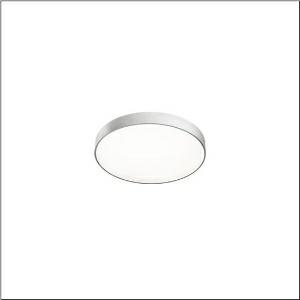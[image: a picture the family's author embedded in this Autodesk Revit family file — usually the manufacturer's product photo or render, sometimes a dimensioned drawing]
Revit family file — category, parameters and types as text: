
# Revit family: round_21_s_51mr34gd0321s
name_source: partatom
category: Lighting Fixtures
units: mm (PartAtom-declared; Revit-internal decimal feet)

## family parameters
Cut with Voids When Loaded = No
Host = Face
Light Source = No
Part Type = Normal
Room Calculation Point = No
Round Connector Dimension = Use Diameter
Shared = No

## types (1)
- Round 21 S (1 x LED, 3930 lm, 28.3 W, 3000K)
    Apparent Load = 28 VA
    CIE Flux Codes = 49 80 96 79 100
    Color Rendering = 80
    Color Temperature = 3000K
    Default Elevation = 1800 mm
    Description = Round 21 S, wall and ceiling luminaire, primary optical cover: cover, of PMMA, opal, light emission: direct/indirect distribution, primary light characteristic: symmetric, installation type: suspended mounting, surface-mounted, LED, rated luminous flux: 3.930lm, luminous efficacy: 139lm/W, light colour: 830, colour temperature: 3000K, control gear: DALI 2, with terminal, 5-pole, mains connection: 230V, AC, 50/60Hz, rated input power: 28.3W, housing, of aluminium, coated, silver, diameter: 400mm, height: 62mm, protection rating (complete): IP40, insulation class (complete): insulation class I (protective earthing), certification: CE, impact resistance: IK04, permissible operating ambient temperature: -10..+35°C, packaging unit: 1 piece
    Height = 87 mm
    Lamp = 1 x LED
    Lamp Light Flux = 3930 lm
    Lamp Power = 28.3 W
    Lamp count = 1
    Length = 400 mm
    Luminous efficacy = 139 lm/W
    Manufacturer = Siteco
    ModVariant = No
    Model = 51MR34GD0321S
    Mounting Place = Ceiling
    Mounting Type = Surface mounted
    Number of Poles = 1
    OnlyDefault = Yes
    Power Factor = 1
    Product Name = Round 21 S
    Product group = wall and ceiling luminaire
    ProductGroupID = 304
    Protection Class = Protection class I
    Protection Degree = IP 40
    RLX_Detail_Level = 1
    RLX_Emergency_Light_Flux = 0 lm
    RLX_Emergency_Type = 0
    RLX_Emergency_Type_DB = No
    RlxData = <blob elided: 11569 chars, md5=6dfd9ba3>
    Socket = socket
    Standby Power = 0 W
    System Light Flux = 3930 lm
    System Power = 28 W
    Type Comments = Product without accessories
    Type Image = l_1258309.jpg
    URL = http://relux.com
    VarID = ---
    Voltage = 0 V
    Weight = 0.00 kg
    Width = 0 mm  [stored 0 ft]

note: [stored X ft] marks values corroborated as IEEE doubles in the binary element streams (Revit-internal decimal feet)

## geometry (parser evidence)
native form markers: Sweep x13
no freeform markers — native parametric forms only
